# Revit family: GRAS_HWG-33 ZWN-R 20-30
name_source: partatom
category: Osprzęt hydrauliczny
revit_build: Autodesk Revit 2018 (Build: 20190510_1515(x64)
units: mm (PartAtom-declared; Revit-internal decimal feet)

## family parameters
Obiekt nadrzędny = Powierzchnia
Punkt obliczania pomieszczeń = Nie
Tnij formami wycięć po wczytaniu = Nie
Typ części = Normalny
Współdzielony = Nie
Wymiar okrągłego złącza = Użyj średnicy

## types (2) — shared parameters
Cabinet material = DC01, RAL3000
Diameter = 650 mm  [stored 2.13255 ft]
Hose_color = Black
K Factor = 42
Opis = https://gras.pl
Producent = GRAS PPPH
URL = http://www.gras.pl
zero-valued in all types: Domyślna rzędna

## per-type parameters (varying)
| type | DN | Depth_hose_reel | Flow | Model |
| HW-25N-20/30 ZWN-S, 650x250 | 32 mm | 250 mm  [stored 0.82021 ft] | 114.0 L/s | HW-25N-20/30, 600x170 |
| HW-25N-20/30 ZWN-S, 650x110 | 25 mm  [stored 0.082021 ft] | 110 mm | 60.0 L/s | HW-25N-20/30, 650x110 |

note: [stored X ft] marks values corroborated as IEEE doubles in the binary element streams (Revit-internal decimal feet)

## geometry (parser evidence)
native form markers: Blend x8
no freeform markers — native parametric forms only
